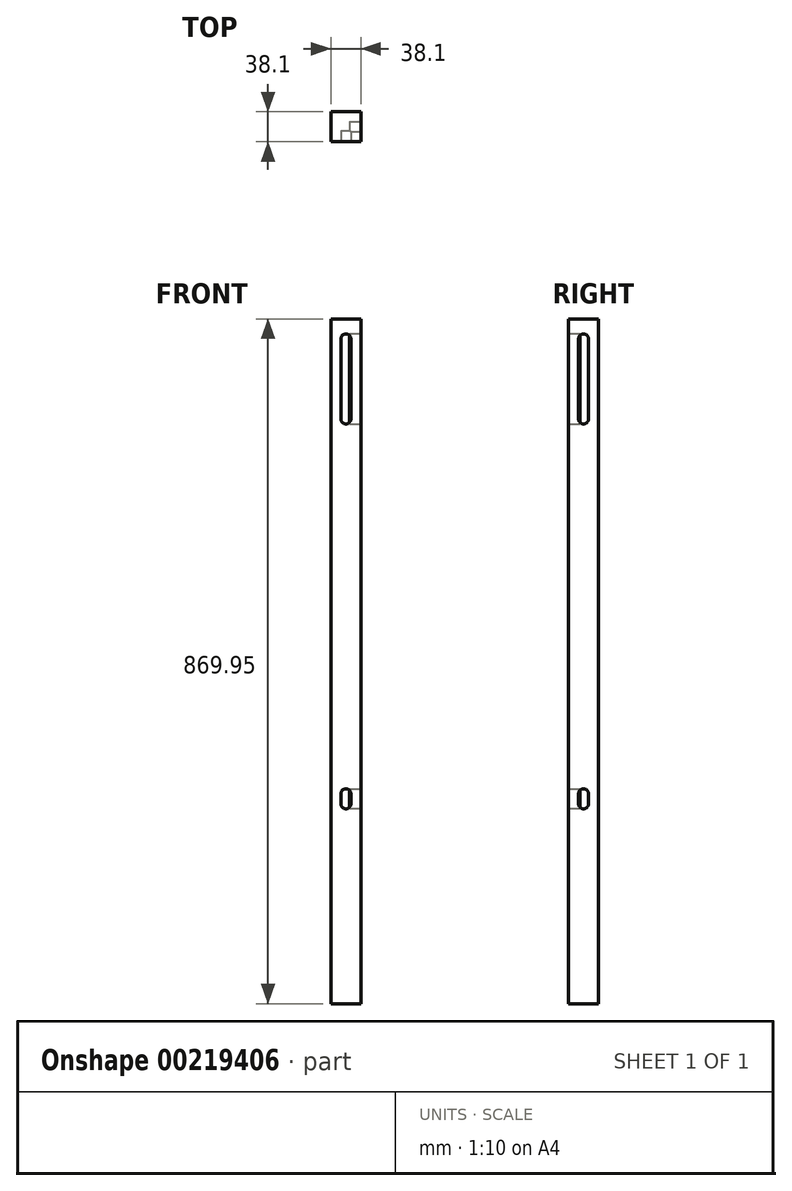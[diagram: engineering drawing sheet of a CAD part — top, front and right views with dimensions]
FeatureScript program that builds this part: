
annotation { "Feature Type Name" : "Feature", "Feature Type Description" : "" }
export const myFeature = defineFeature(function(context is Context, id is Id, definition is map)
    precondition{}
    {
        {
            var Q0;
            Q0=qCreatedBy(makeId("Top.planeOp"),FACE);
            var sketch = newSketch(context, id + "F0", { "sketchPlane" : qUnion([Q0])});
            skLineSegment(sketch, "E0.bottom", {"start": v(19.05, -19.05) * mm, "end": v(-19.05, -19.05) * mm});
            skLineSegment(sketch, "E0.top", {"start": v(19.05, 19.05) * mm, "end": v(-19.05, 19.05) * mm});
            skLineSegment(sketch, "E0.left", {"start": v(19.05, -19.05) * mm, "end": v(19.05, 19.05) * mm});
            skLineSegment(sketch, "E0.right", {"start": v(-19.05, -19.05) * mm, "end": v(-19.05, 19.05) * mm});
            skPoint(sketch, "E0.middle", {"position": v(0, 0) * mm});
            skSolve(sketch);
        }
        {
            var Q0;
            Q0 = qSketchRegion(id + "F0", true);
            extrude(context, id + "F1", {"entities" : qUnion([Q0]), "oppositeDirection" : true, "depth" : 869.95 * mm, "offsetDistance" : 25.4 * mm});
        }
        {
            var Q0;
            Q0=makeQuery(id+"F1.opExtrude","SWEPT_FACE",FACE,{"disambiguationData":[OSD([sQuery(id+"F0.wireOp",EDGE,"E0.bottom")])]});
            var sketch = newSketch(context, id + "F2", { "sketchPlane" : qUnion([Q0])});
            skLineSegment(sketch, "E1.bottom", {"start": v(6.35, -133.35) * mm, "end": v(-6.35, -133.35) * mm});
            skLineSegment(sketch, "E1.top", {"start": v(6.35, -19.05) * mm, "end": v(-6.35, -19.05) * mm});
            skLineSegment(sketch, "E1.left", {"start": v(6.35, -133.35) * mm, "end": v(6.35, -19.05) * mm});
            skLineSegment(sketch, "E1.right", {"start": v(-6.35, -133.35) * mm, "end": v(-6.35, -19.05) * mm});
            skPoint(sketch, "E1.middle", {"position": v(0, -76.2) * mm});
            skLineSegment(sketch, "E2.bottom", {"start": v(-6.35, -622.3) * mm, "end": v(6.35, -622.3) * mm});
            skLineSegment(sketch, "E2.top", {"start": v(-6.35, -596.9) * mm, "end": v(6.35, -596.9) * mm});
            skLineSegment(sketch, "E2.left", {"start": v(-6.35, -622.3) * mm, "end": v(-6.35, -596.9) * mm});
            skLineSegment(sketch, "E2.right", {"start": v(6.35, -622.3) * mm, "end": v(6.35, -596.9) * mm});
            skPoint(sketch, "E2.middle", {"position": v(0, -609.6) * mm});
            skSolve(sketch);
        }
        {
            var Q0;
            Q0 = qSketchRegion(id + "F2", true);
            extrude(context, id + "F3", {"entities" : qUnion([Q0]), "operationType" : NewBodyOperationType.REMOVE, "oppositeDirection" : true, "depth" : 14.29 * mm, "offsetDistance" : 25.4 * mm});
        }
        {
            var Q0;
            Q0=makeQuery(id+"F1.opExtrude","SWEPT_FACE",FACE,{"disambiguationData":[OSD([sQuery(id+"F0.wireOp",EDGE,"E0.left")])]});
            var sketch = newSketch(context, id + "F4", { "sketchPlane" : qUnion([Q0])});
            skLineSegment(sketch, "E3.bottom", {"start": v(-6.35, -133.35) * mm, "end": v(6.35, -133.35) * mm});
            skLineSegment(sketch, "E3.top", {"start": v(-6.35, -19.05) * mm, "end": v(6.35, -19.05) * mm});
            skLineSegment(sketch, "E3.left", {"start": v(-6.35, -133.35) * mm, "end": v(-6.35, -19.05) * mm});
            skLineSegment(sketch, "E3.right", {"start": v(6.35, -133.35) * mm, "end": v(6.35, -19.05) * mm});
            skPoint(sketch, "E3.middle", {"position": v(0, -76.2) * mm});
            skLineSegment(sketch, "E4.bottom", {"start": v(-6.35, -596.9) * mm, "end": v(6.35, -596.9) * mm});
            skLineSegment(sketch, "E4.top", {"start": v(-6.35, -622.3) * mm, "end": v(6.35, -622.3) * mm});
            skLineSegment(sketch, "E4.left", {"start": v(-6.35, -596.9) * mm, "end": v(-6.35, -622.3) * mm});
            skLineSegment(sketch, "E4.right", {"start": v(6.35, -596.9) * mm, "end": v(6.35, -622.3) * mm});
            skPoint(sketch, "E4.middle", {"position": v(0, -609.6) * mm});
            skSolve(sketch);
        }
        {
            var Q0;
            Q0 = qSketchRegion(id + "F4", true);
            extrude(context, id + "F5", {"entities" : qUnion([Q0]), "operationType" : NewBodyOperationType.REMOVE, "oppositeDirection" : true, "depth" : 14.29 * mm, "offsetDistance" : 25.4 * mm});
        }
        {
            var Q0;
            Q0=makeQuery(id+"F3.boolean.opBoolean","COPY",EDGE,{"derivedFrom":makeQuery(id+"F3.opExtrude","SWEPT_EDGE",EDGE,{"disambiguationData":[OSD([sQuery(id+"F2.wireOp",EDGE,"E1.top"),sQuery(id+"F2.wireOp",EDGE,"E1.right")])]})});
            var Q1;
            Q1=makeQuery(id+"F3.boolean.opBoolean","COPY",EDGE,{"derivedFrom":makeQuery(id+"F3.opExtrude","SWEPT_EDGE",EDGE,{"disambiguationData":[OSD([sQuery(id+"F2.wireOp",EDGE,"E1.top"),sQuery(id+"F2.wireOp",EDGE,"E1.left")])]})});
            var Q2;
            Q2=makeQuery(id+"F3.boolean.opBoolean","COPY",EDGE,{"derivedFrom":makeQuery(id+"F3.opExtrude","SWEPT_EDGE",EDGE,{"disambiguationData":[OSD([sQuery(id+"F2.wireOp",EDGE,"E1.bottom"),sQuery(id+"F2.wireOp",EDGE,"E1.right")])]})});
            var Q3;
            Q3=makeQuery(id+"F3.boolean.opBoolean","COPY",EDGE,{"derivedFrom":makeQuery(id+"F3.opExtrude","SWEPT_EDGE",EDGE,{"disambiguationData":[OSD([sQuery(id+"F2.wireOp",EDGE,"E1.bottom"),sQuery(id+"F2.wireOp",EDGE,"E1.left")])]})});
            var Q4;
            Q4=makeQuery(id+"F5.boolean.opBoolean","COPY",EDGE,{"derivedFrom":makeQuery(id+"F5.opExtrude","SWEPT_EDGE",EDGE,{"disambiguationData":[OSD([sQuery(id+"F4.wireOp",EDGE,"E3.bottom"),sQuery(id+"F4.wireOp",EDGE,"E3.right")])]})});
            var Q5;
            Q5=makeQuery(id+"F5.boolean.opBoolean","COPY",EDGE,{"derivedFrom":makeQuery(id+"F5.opExtrude","SWEPT_EDGE",EDGE,{"disambiguationData":[OSD([sQuery(id+"F4.wireOp",EDGE,"E3.bottom"),sQuery(id+"F4.wireOp",EDGE,"E3.left")])]})});
            var Q6;
            Q6=makeQuery(id+"F5.boolean.opBoolean","COPY",EDGE,{"derivedFrom":makeQuery(id+"F5.opExtrude","SWEPT_EDGE",EDGE,{"disambiguationData":[OSD([sQuery(id+"F4.wireOp",EDGE,"E3.top"),sQuery(id+"F4.wireOp",EDGE,"E3.right")])]})});
            var Q7;
            Q7=makeQuery(id+"F5.boolean.opBoolean","COPY",EDGE,{"derivedFrom":makeQuery(id+"F5.opExtrude","SWEPT_EDGE",EDGE,{"disambiguationData":[OSD([sQuery(id+"F4.wireOp",EDGE,"E3.top"),sQuery(id+"F4.wireOp",EDGE,"E3.left")])]})});
            var Q8;
            Q8=makeQuery(id+"F3.boolean.opBoolean","COPY",EDGE,{"derivedFrom":makeQuery(id+"F3.opExtrude","SWEPT_EDGE",EDGE,{"disambiguationData":[OSD([sQuery(id+"F2.wireOp",EDGE,"E2.top"),sQuery(id+"F2.wireOp",EDGE,"E2.left")])]})});
            var Q9;
            Q9=makeQuery(id+"F3.boolean.opBoolean","COPY",EDGE,{"derivedFrom":makeQuery(id+"F3.opExtrude","SWEPT_EDGE",EDGE,{"disambiguationData":[OSD([sQuery(id+"F2.wireOp",EDGE,"E2.top"),sQuery(id+"F2.wireOp",EDGE,"E2.right")])]})});
            var Q10;
            Q10=makeQuery(id+"F3.boolean.opBoolean","COPY",EDGE,{"derivedFrom":makeQuery(id+"F3.opExtrude","SWEPT_EDGE",EDGE,{"disambiguationData":[OSD([sQuery(id+"F2.wireOp",EDGE,"E2.bottom"),sQuery(id+"F2.wireOp",EDGE,"E2.left")])]})});
            var Q11;
            Q11=makeQuery(id+"F3.boolean.opBoolean","COPY",EDGE,{"derivedFrom":makeQuery(id+"F3.opExtrude","SWEPT_EDGE",EDGE,{"disambiguationData":[OSD([sQuery(id+"F2.wireOp",EDGE,"E2.bottom"),sQuery(id+"F2.wireOp",EDGE,"E2.right")])]})});
            var Q12;
            Q12=makeQuery(id+"F5.boolean.opBoolean","COPY",EDGE,{"derivedFrom":makeQuery(id+"F5.opExtrude","SWEPT_EDGE",EDGE,{"disambiguationData":[OSD([sQuery(id+"F4.wireOp",EDGE,"E4.bottom"),sQuery(id+"F4.wireOp",EDGE,"E4.left")])]})});
            var Q13;
            Q13=makeQuery(id+"F5.boolean.opBoolean","COPY",EDGE,{"derivedFrom":makeQuery(id+"F5.opExtrude","SWEPT_EDGE",EDGE,{"disambiguationData":[OSD([sQuery(id+"F4.wireOp",EDGE,"E4.bottom"),sQuery(id+"F4.wireOp",EDGE,"E4.right")])]})});
            var Q14;
            Q14=makeQuery(id+"F5.boolean.opBoolean","COPY",EDGE,{"derivedFrom":makeQuery(id+"F5.opExtrude","SWEPT_EDGE",EDGE,{"disambiguationData":[OSD([sQuery(id+"F4.wireOp",EDGE,"E4.top"),sQuery(id+"F4.wireOp",EDGE,"E4.left")])]})});
            var Q15;
            Q15=makeQuery(id+"F5.boolean.opBoolean","COPY",EDGE,{"derivedFrom":makeQuery(id+"F5.opExtrude","SWEPT_EDGE",EDGE,{"disambiguationData":[OSD([sQuery(id+"F4.wireOp",EDGE,"E4.top"),sQuery(id+"F4.wireOp",EDGE,"E4.right")])]})});
            fillet(context, id + "F6", {"entities" : qUnion([Q0, Q1, Q2, Q3, Q4, Q5, Q6, Q7, Q8, Q9, Q10, Q11, Q12, Q13, Q14, Q15]), "radius" : 6.35 * mm, "tangentPropagation" : true, "allowEdgeOverflow" : false});
        }
    });
